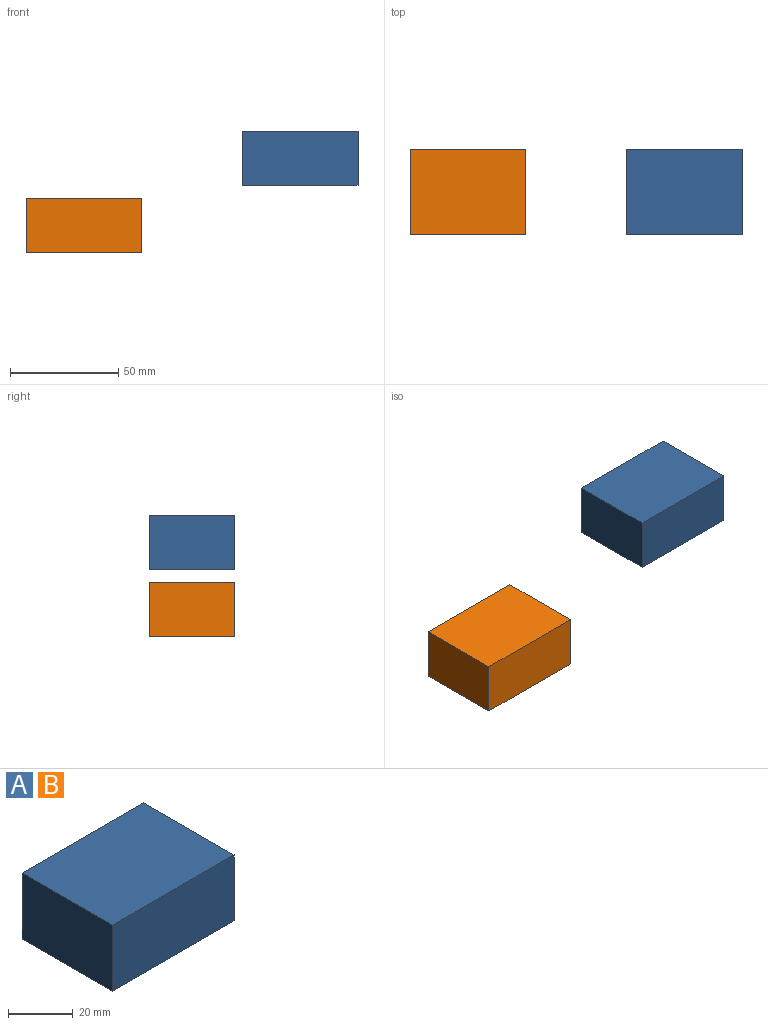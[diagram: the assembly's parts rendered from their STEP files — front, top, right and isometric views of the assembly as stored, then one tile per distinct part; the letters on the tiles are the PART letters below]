
ASSEMBLY  parts=2 mates=1
PART A: 6 faces, bbox 53.2x39.5x25 mm
  f0: plane 53.22x25mm, normal (0,1,0), area 1330.6mm2, adj f1,f3,f4,f5
  f1: plane 39.53x25mm, normal (-1,0,0), area 988.3mm2, adj f0,f2,f4,f5
  f2: plane 53.22x25mm, normal (0,-1,0), area 1330.6mm2, adj f1,f3,f4,f5
  f3: plane 39.53x25mm, normal (1,0,0), area 988.3mm2, adj f0,f2,f4,f5
  f4: plane 53.22x39.53mm, normal (0,0,1), area 2104mm2, adj f0,f1,f2,f3
  f5: plane 53.22x39.53mm, normal (0,0,-1), area 2104mm2, adj f0,f1,f2,f3
PART B: same geometry as A
PLACE A t=(-62.42,-17.12,7.26)mm fixed
PLACE B t=(-162.42,-17.12,-23.96)mm
MATE slider A.f4 <-> B.f4  axis (0,0,1) through (-97.56,-43.15,32.26)mm
